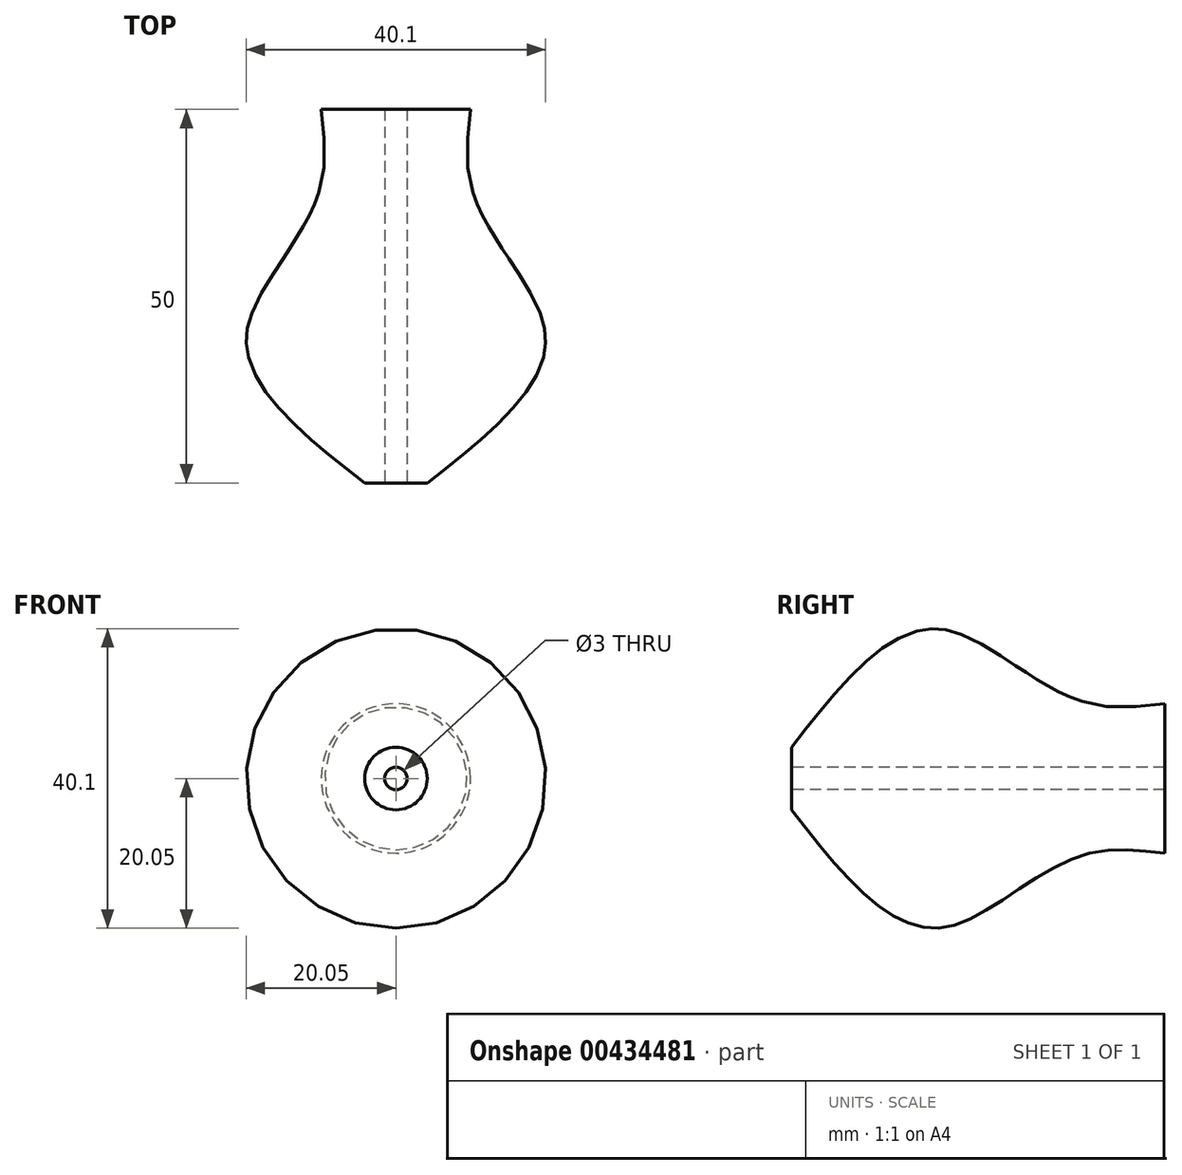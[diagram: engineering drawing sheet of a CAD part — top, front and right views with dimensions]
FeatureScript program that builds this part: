
annotation { "Feature Type Name" : "Feature", "Feature Type Description" : "" }
export const myFeature = defineFeature(function(context is Context, id is Id, definition is map)
    precondition{}
    {
        {
            var Q0;
            Q0=qCreatedBy(makeId("Front.planeOp"),FACE);
            cPlane(context, id + "F0", {"entities" : qUnion([Q0]), "cplaneType" : CPlaneType.OFFSET, "offset" : 30 * mm, "width" : 150 * mm, "height" : 150 * mm});
        }
        {
            var Q0;
            Q0=qCreatedBy(makeId("Front.planeOp"),FACE);
            cPlane(context, id + "F1", {"entities" : qUnion([Q0]), "cplaneType" : CPlaneType.OFFSET, "offset" : 10 * mm, "width" : 150 * mm, "height" : 150 * mm});
        }
        {
            var Q0;
            Q0=qCreatedBy(makeId("Front.planeOp"),FACE);
            var sketch = newSketch(context, id + "F2", { "sketchPlane" : qUnion([Q0])});
            skCircle(sketch, "E0", {"center": v(0, 0) * mm, "radius": 10 * mm});
            skSolve(sketch);
        }
        {
            var Q0;
            Q0=qCreatedBy(id+"F1.planeOp",FACE);
            var sketch = newSketch(context, id + "F3", { "sketchPlane" : qUnion([Q0])});
            skCircle(sketch, "E1", {"center": v(0, 0) * mm, "radius": 10 * mm});
            skSolve(sketch);
        }
        {
            var Q0;
            Q0=qCreatedBy(id+"F0.planeOp",FACE);
            var sketch = newSketch(context, id + "F4", { "sketchPlane" : qUnion([Q0])});
            skCircle(sketch, "E2", {"center": v(0, 0) * mm, "radius": 20 * mm});
            skSolve(sketch);
        }
        {
            var Q0;
            Q0=qCreatedBy(makeId("Front.planeOp"),FACE);
            cPlane(context, id + "F5", {"entities" : qUnion([Q0]), "cplaneType" : CPlaneType.OFFSET, "offset" : 50 * mm, "width" : 150 * mm, "height" : 150 * mm});
        }
        {
            var Q0;
            Q0=qCreatedBy(id+"F5.planeOp",FACE);
            var sketch = newSketch(context, id + "F6", { "sketchPlane" : qUnion([Q0])});
            skCircle(sketch, "E3", {"center": v(0, 0) * mm, "radius": 4.2 * mm});
            skSolve(sketch);
        }
        {
            var Q0;
            Q0=makeQuery(id+"F2.imprint","IMPRINT",FACE,{"disambiguationData":[TD([[makeQuery(id+"F2.imprint","IMPRINT",EDGE,{"derivedFrom":sQuery(id+"F2.wireOp",EDGE,"E0")}),1.0]])]});
            var Q1;
            Q1=makeQuery(id+"F3.imprint","IMPRINT",FACE,{"disambiguationData":[TD([[makeQuery(id+"F3.imprint","IMPRINT",EDGE,{"derivedFrom":sQuery(id+"F3.wireOp",EDGE,"E1")}),1.0]])]});
            var Q2;
            Q2=makeQuery(id+"F4.imprint","IMPRINT",FACE,{"disambiguationData":[TD([[makeQuery(id+"F4.imprint","IMPRINT",EDGE,{"derivedFrom":sQuery(id+"F4.wireOp",EDGE,"E2")}),1.0]])]});
            var Q3;
            Q3=makeQuery(id+"F6.imprint","IMPRINT",FACE,{"disambiguationData":[TD([[makeQuery(id+"F6.imprint","IMPRINT",EDGE,{"derivedFrom":sQuery(id+"F6.wireOp",EDGE,"E3")}),1.0]])]});
            loft(context, id + "F7", {"sheetProfilesArray" : [{ "sheetProfileEntities" : qUnion([Q0]) }, { "sheetProfileEntities" : qUnion([Q1]) }, { "sheetProfileEntities" : qUnion([Q2]) }, { "sheetProfileEntities" : qUnion([Q3]) }]});
        }
        {
            var Q0;
            Q0=makeQuery(id+"F7.opLoft","CAP_FACE",FACE,{"disambiguationData":[OSD([makeQuery(id+"F6.imprint","IMPRINT",FACE,{"disambiguationData":[TD([[makeQuery(id+"F6.imprint","IMPRINT",EDGE,{"derivedFrom":sQuery(id+"F6.wireOp",EDGE,"E3")}),1.0]])]})])],"isStart":true});
            var sketch = newSketch(context, id + "F8", { "sketchPlane" : qUnion([Q0])});
            skCircle(sketch, "E4", {"center": v(0, 0) * mm, "radius": 1.5 * mm});
            skSolve(sketch);
        }
        {
            var Q0;
            Q0=makeQuery(id+"F8.imprint","IMPRINT",FACE,{"disambiguationData":[TD([[makeQuery(id+"F8.imprint","IMPRINT",EDGE,{"derivedFrom":sQuery(id+"F8.wireOp",EDGE,"E4")}),1.0]])]});
            extrude(context, id + "F9", {"entities" : qUnion([Q0]), "operationType" : NewBodyOperationType.REMOVE, "oppositeDirection" : true, "depth" : 61.2 * mm});
        }
    });
